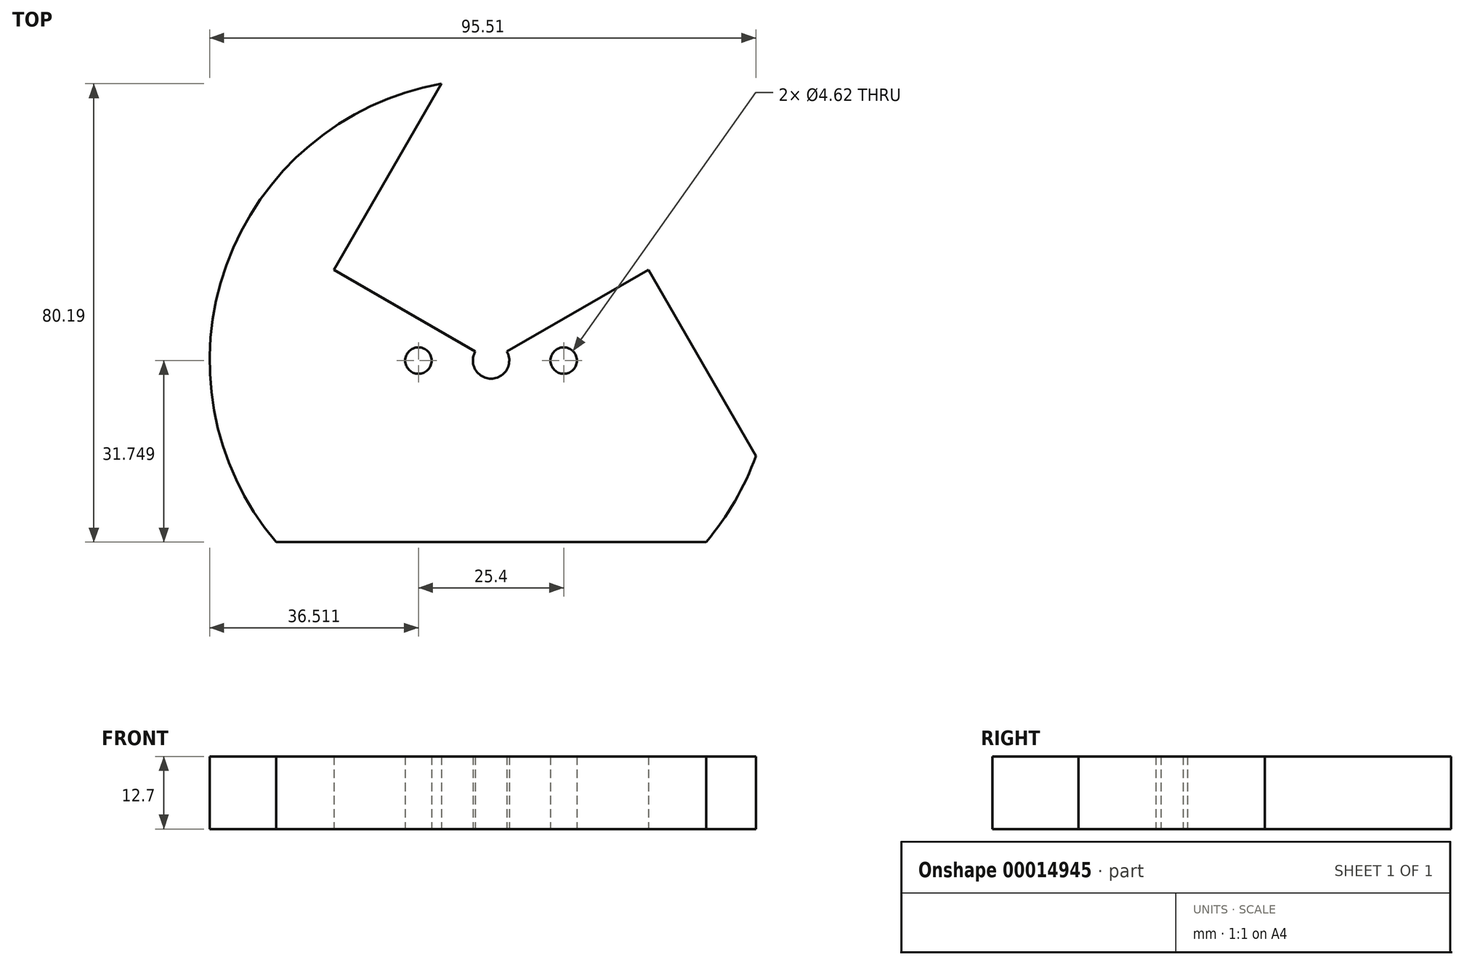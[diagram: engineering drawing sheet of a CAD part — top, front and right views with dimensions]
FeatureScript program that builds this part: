
annotation { "Feature Type Name" : "Feature", "Feature Type Description" : "" }
export const myFeature = defineFeature(function(context is Context, id is Id, definition is map)
    precondition{}
    {
        {
            var Q0;
            Q0=qCreatedBy(makeId("Top.planeOp"),FACE);
            var sketch = newSketch(context, id + "F0", { "sketchPlane" : qUnion([Q0])});
            skCircle(sketch, "E0", {"center": v(55, 31.75) * mm, "radius": 49.21 * mm});
            skLineSegment(sketch, "E1", {"start": v(0, 0) * mm, "end": v(55, 95.25) * mm});
            skLineSegment(sketch, "E2", {"start": v(55, 95.25) * mm, "end": v(109.98, 0) * mm});
            skLineSegment(sketch, "E3", {"start": v(109.98, 0) * mm, "end": v(0, 0) * mm});
            skPoint(sketch, "E4", {"position": v(0, 0) * mm});
            skLineSegment(sketch, "E5", {"start": v(55, 0) * mm, "end": v(55, 31.75) * mm});
            skLineSegment(sketch, "E6", {"start": v(27.5, 47.62) * mm, "end": v(55, 31.75) * mm});
            skLineSegment(sketch, "E7", {"start": v(82.49, 47.62) * mm, "end": v(55, 31.75) * mm});
            skCircle(sketch, "E8", {"center": v(55, 31.75) * mm, "radius": 3.18 * mm});
            skCircle(sketch, "E9", {"center": v(42.3, 31.75) * mm, "radius": 2.31 * mm});
            skCircle(sketch, "E10", {"center": v(67.7, 31.75) * mm, "radius": 2.31 * mm});
            skSolve(sketch);
        }
        {
            var Q0;
            Q0=makeQuery(id+"F0.imprint","IMPRINT",FACE,{"disambiguationData":[TD([[makeQuery(id+"F0.imprint","IMPRINT",EDGE,{"derivedFrom":sQuery(id+"F0.wireOp",EDGE,"E9")}),-1.0]])]});
            var Q1;
            {var subQ5=sQuery(id+"F0.wireOp",EDGE,"E1");var subQ8=sQuery(id+"F0.wireOp",EDGE,"E0");var subQ11=makeQuery(id+"F0.imprint","INTERSECT",VERTEX,{"disambiguationData":[OD(0.0)],"derivedFrom":[subQ8,subQ5]});Q1=makeQuery(id+"F0.imprint","IMPRINT",FACE,{"disambiguationData":[TD([[makeQuery(id+"F0.imprint","IMPRINT",EDGE,{"disambiguationData":[TD([[subQ11,1.0]])],"derivedFrom":subQ8}),1.0]])]});}
            var Q2;
            Q2=makeQuery(id+"F0.imprint","IMPRINT",FACE,{"disambiguationData":[TD([[makeQuery(id+"F0.imprint","IMPRINT",EDGE,{"derivedFrom":sQuery(id+"F0.wireOp",EDGE,"E10")}),-1.0]])]});
            extrude(context, id + "F1", {"entities" : qUnion([Q0, Q1, Q2]), "depth" : 12.7 * mm});
        }
    });
